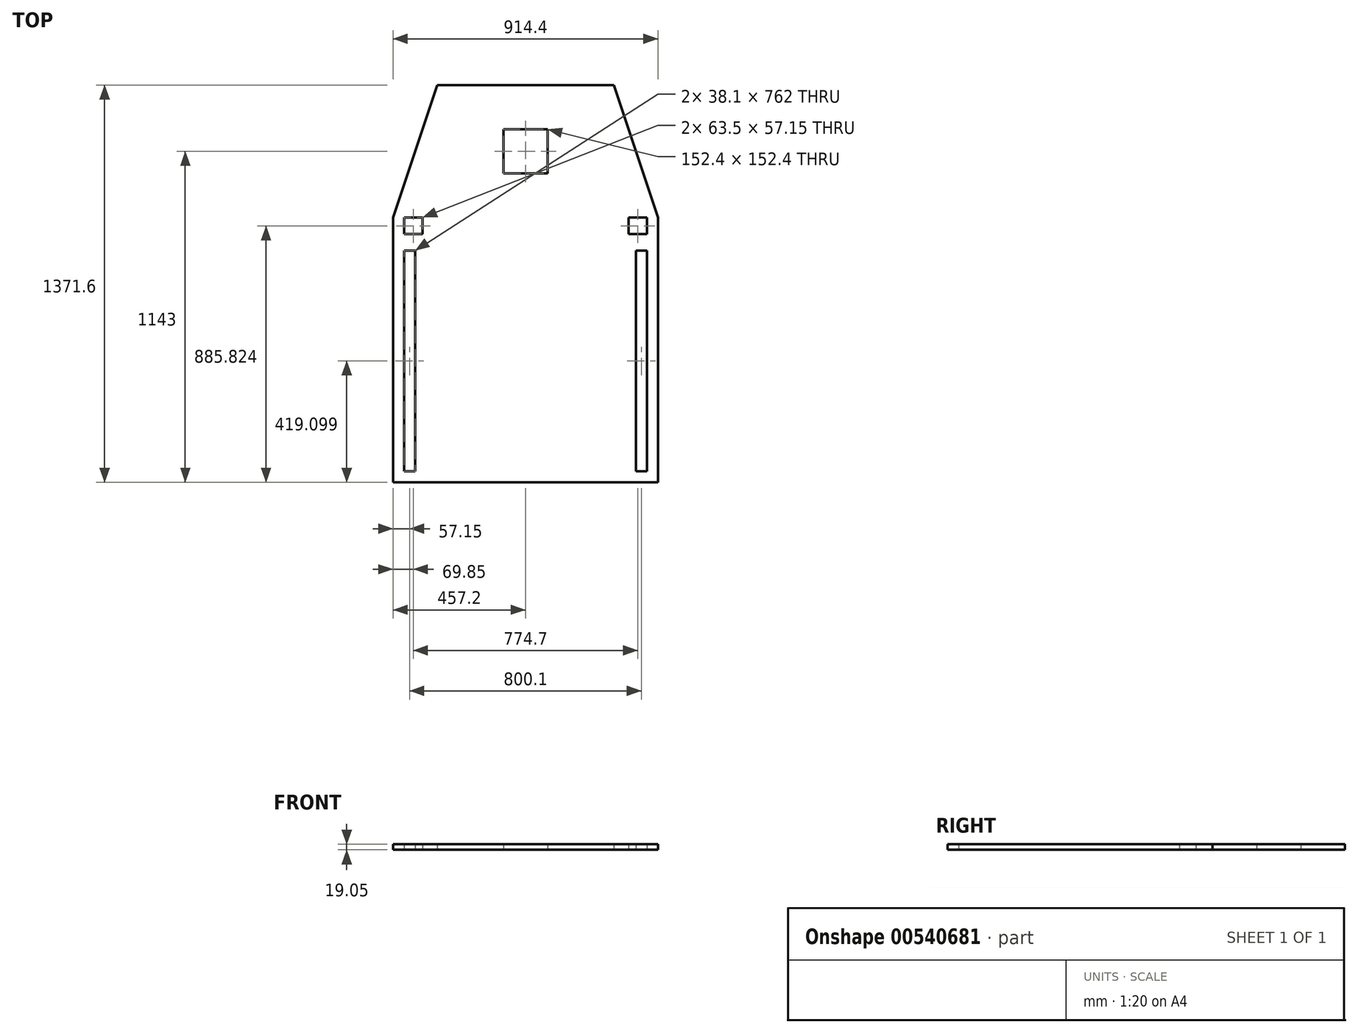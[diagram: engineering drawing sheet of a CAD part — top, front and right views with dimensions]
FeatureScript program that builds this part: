
annotation { "Feature Type Name" : "Feature", "Feature Type Description" : "" }
export const myFeature = defineFeature(function(context is Context, id is Id, definition is map)
    precondition{}
    {
        {
            var Q0;
            Q0=qCreatedBy(makeId("Top.planeOp"),FACE);
            var sketch = newSketch(context, id + "F0", { "sketchPlane" : qUnion([Q0])});
            skLineSegment(sketch, "E0.top", {"start": v(-669.86, -508.86) * mm, "end": v(244.54, -508.86) * mm});
            skLineSegment(sketch, "E0.left", {"start": v(-669.86, 405.54) * mm, "end": v(-669.86, -508.86) * mm});
            skLineSegment(sketch, "E0.right", {"start": v(244.54, 405.54) * mm, "end": v(244.54, -508.86) * mm});
            skLineSegment(sketch, "E1", {"start": v(-517.46, 862.74) * mm, "end": v(-669.86, 405.54) * mm});
            skLineSegment(sketch, "E2", {"start": v(92.14, 862.74) * mm, "end": v(244.54, 405.54) * mm});
            skLineSegment(sketch, "E3.0", {"start": v(-631.76, 291.24) * mm, "end": v(-631.76, -470.76) * mm});
            skLineSegment(sketch, "E4.0", {"start": v(206.44, 291.24) * mm, "end": v(206.44, -470.76) * mm});
            skLineSegment(sketch, "E5.0", {"start": v(-631.76, -470.76) * mm, "end": v(-593.66, -470.76) * mm});
            skLineSegment(sketch, "E6.0", {"start": v(-593.66, 291.24) * mm, "end": v(-593.66, -470.76) * mm});
            skLineSegment(sketch, "E7.0", {"start": v(168.34, 291.24) * mm, "end": v(168.34, -470.76) * mm});
            skLineSegment(sketch, "E8", {"start": v(-631.76, 291.24) * mm, "end": v(-593.66, 291.24) * mm});
            skLineSegment(sketch, "E9", {"start": v(168.34, 291.24) * mm, "end": v(206.44, 291.24) * mm});
            skLineSegment(sketch, "E10.trimOffspring", {"start": v(168.34, -470.76) * mm, "end": v(206.44, -470.76) * mm});
            skLineSegment(sketch, "E11", {"start": v(-631.76, 405.54) * mm, "end": v(-568.26, 405.54) * mm});
            skLineSegment(sketch, "E12", {"start": v(-631.76, 348.39) * mm, "end": v(-631.76, 405.54) * mm});
            skLineSegment(sketch, "E13", {"start": v(206.44, 348.39) * mm, "end": v(206.44, 405.54) * mm});
            skLineSegment(sketch, "E14", {"start": v(-631.76, 348.39) * mm, "end": v(-568.26, 348.39) * mm});
            skLineSegment(sketch, "E15.0", {"start": v(-568.26, 348.39) * mm, "end": v(-568.26, 405.54) * mm});
            skLineSegment(sketch, "E16.0", {"start": v(142.94, 348.39) * mm, "end": v(142.94, 405.54) * mm});
            skLineSegment(sketch, "E17.trimOffspring", {"start": v(142.94, 348.39) * mm, "end": v(206.44, 348.39) * mm});
            skLineSegment(sketch, "E18.trimOffspring", {"start": v(142.94, 405.54) * mm, "end": v(206.44, 405.54) * mm});
            skLineSegment(sketch, "E19", {"start": v(-517.46, 862.74) * mm, "end": v(92.14, 862.74) * mm});
            skLineSegment(sketch, "E20.0", {"start": v(-288.86, 710.34) * mm, "end": v(-136.46, 710.34) * mm});
            skLineSegment(sketch, "E21.0", {"start": v(-288.86, 557.94) * mm, "end": v(-136.46, 557.94) * mm});
            skLineSegment(sketch, "E22.0", {"start": v(-288.86, 557.94) * mm, "end": v(-288.86, 710.34) * mm});
            skLineSegment(sketch, "E23.0", {"start": v(-136.46, 557.94) * mm, "end": v(-136.46, 710.34) * mm});
            skSolve(sketch);
        }
        {
            var Q0;
            Q0=makeQuery(id+"F0.imprint","IMPRINT",FACE,{"disambiguationData":[TD([[makeQuery(id+"F0.imprint","IMPRINT",EDGE,{"derivedFrom":sQuery(id+"F0.wireOp",EDGE,"E0.top")}),1.0]])]});
            extrude(context, id + "F1", {"entities" : qUnion([Q0]), "depth" : 19.05 * mm, "offsetDistance" : 25.4 * mm});
        }
    });
